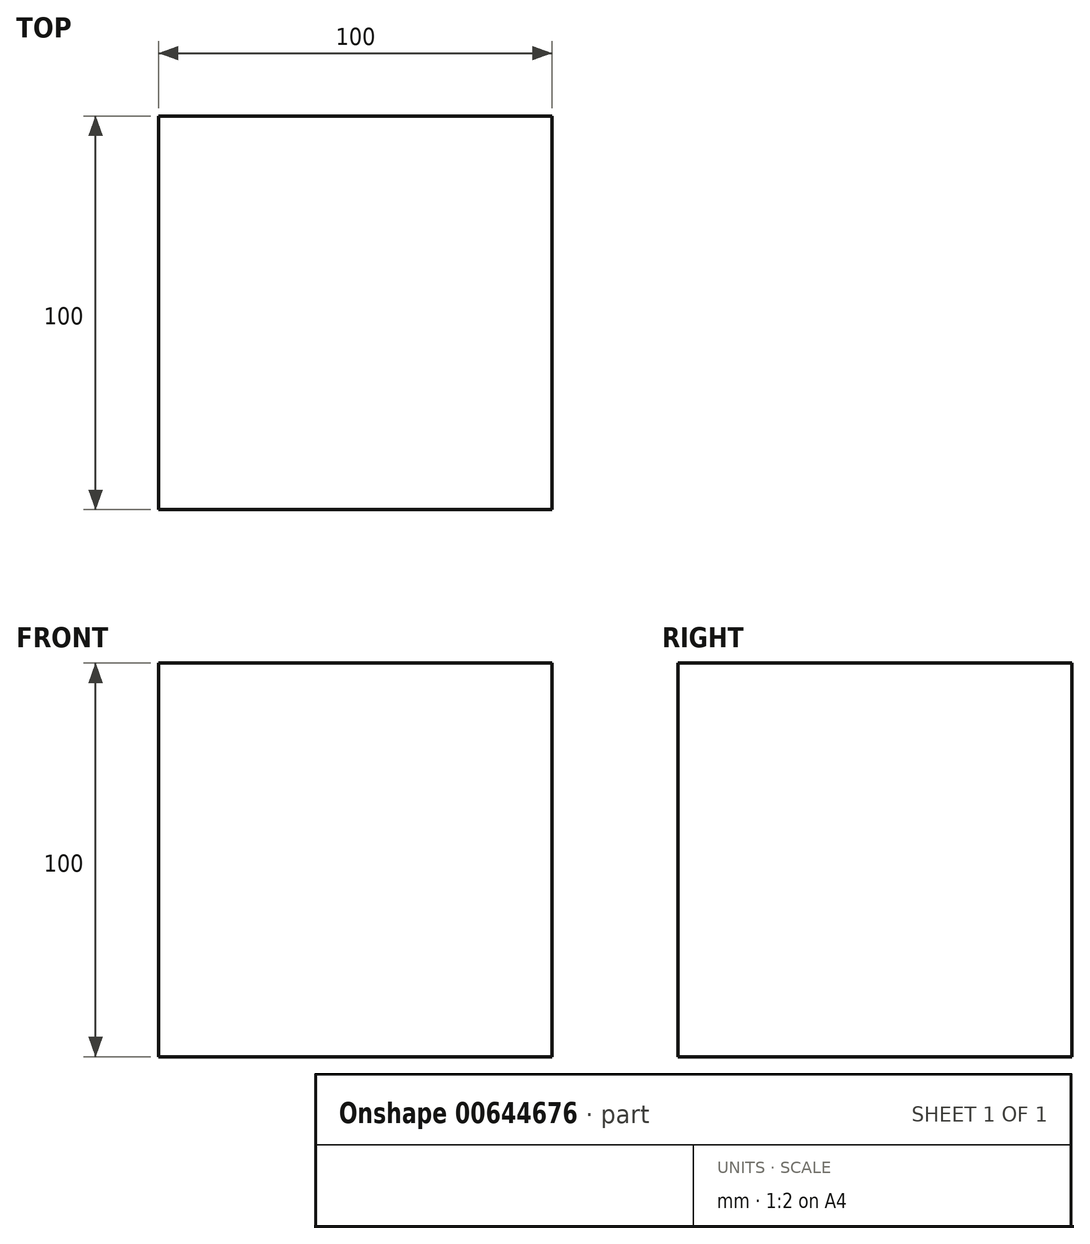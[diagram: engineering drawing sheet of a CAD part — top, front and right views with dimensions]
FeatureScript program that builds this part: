
annotation { "Feature Type Name" : "Feature", "Feature Type Description" : "" }
export const myFeature = defineFeature(function(context is Context, id is Id, definition is map)
    precondition{}
    {
        {
            var Q0;
            Q0=qCreatedBy(makeId("Front.planeOp"),FACE);
            var sketch = newSketch(context, id + "F0", { "sketchPlane" : qUnion([Q0])});
            skLineSegment(sketch, "E0.bottom", {"start": v(0, 0) * mm, "end": v(100, 0) * mm});
            skLineSegment(sketch, "E0.top", {"start": v(0, -100) * mm, "end": v(100, -100) * mm});
            skLineSegment(sketch, "E0.left", {"start": v(0, 0) * mm, "end": v(0, -100) * mm});
            skLineSegment(sketch, "E0.right", {"start": v(100, 0) * mm, "end": v(100, -100) * mm});
            skSolve(sketch);
        }
        {
            var Q0;
            Q0=makeQuery(id+"F0.imprint","IMPRINT",FACE,{"disambiguationData":[TD([[makeQuery(id+"F0.imprint","IMPRINT",EDGE,{"derivedFrom":sQuery(id+"F0.wireOp",EDGE,"E0.bottom")}),-1.0]])]});
            extrude(context, id + "F1", {"entities" : qUnion([Q0]), "depth" : 100 * mm, "offsetDistance" : 25 * mm});
        }
    });
